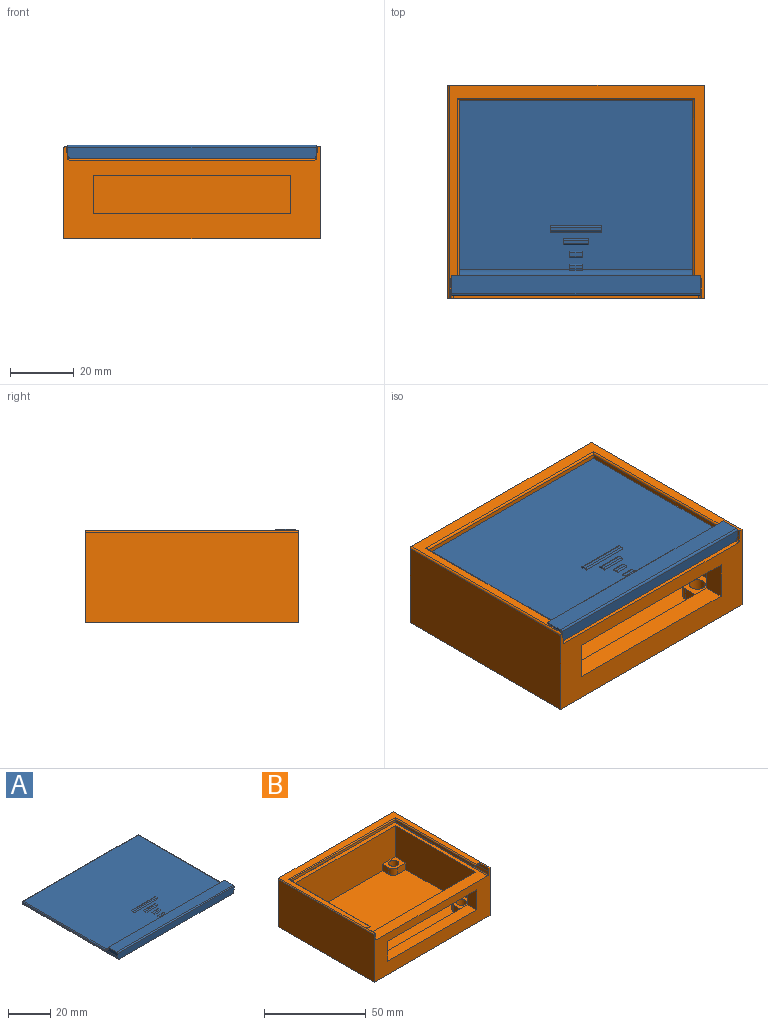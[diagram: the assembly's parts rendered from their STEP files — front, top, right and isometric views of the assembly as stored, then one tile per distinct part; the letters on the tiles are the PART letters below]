
ASSEMBLY  parts=2 mates=1
PART A: 39 faces, bbox 78.7x71.2x4.3 mm
  f0: plane 76.84x55.4mm, normal (0,0,1), area 4194.1mm2, adj f7,f8,f10,f11,f13,f14,f16,f17
  f1: plane 78x3.66mm, normal (0,-1,0), area 284.3mm2, adj f3,f4,f5,f26,f27,f29,f30,f32
  f2: plane 77.9x1.56mm, normal (0,1,0), area 116.2mm2, adj f3,f4,f5,f26,f27,f35,f36,f38
  f3: plane 75.68x64.2mm, normal (0,0,-1), area 4858.5mm2, adj f1,f2,f26,f27
  f4: plane 64.2x1.15mm, normal (-0.99,0,-0.15), area 41.5mm2, adj f1,f2,f27,f29,f34,f35
  f5: plane 64.2x1.15mm, normal (0.99,0,-0.15), area 41.5mm2, adj f1,f2,f26,f30,f37,f38
  f6: plane 4x1mm, normal (0,0,1), area 4mm2, adj f7,f8,f24,f25
  f7: plane 2x0.5mm, normal (-1,0,0), area 0.9mm2, adj f0,f6,f24,f25,f33
  f8: plane 2x0.5mm, normal (1,0,0), area 0.9mm2, adj f0,f6,f24,f25,f33
  f9: plane 4x1mm, normal (0,0,1), area 4mm2, adj f10,f11,f22,f23
  f10: plane 2x0.5mm, normal (-1,0,0), area 0.9mm2, adj f0,f9,f22,f23
  f11: plane 2x0.5mm, normal (1,0,0), area 0.9mm2, adj f0,f9,f22,f23
  f12: plane 8x1mm, normal (0,0,1), area 8mm2, adj f13,f14,f20,f21
  f13: plane 2x0.5mm, normal (-1,0,0), area 0.9mm2, adj f0,f12,f20,f21
  f14: plane 2x0.5mm, normal (1,0,0), area 0.9mm2, adj f0,f12,f20,f21
  f15: plane 16x1mm, normal (0,0,1), area 16mm2, adj f16,f17,f18,f19
  f16: plane 2x0.5mm, normal (-1,0,0), area 0.9mm2, adj f0,f15,f18,f19
  f17: plane 2x0.5mm, normal (1,0,0), area 0.9mm2, adj f0,f15,f18,f19
  f18: cylinder r=0.5mm len=16mm, axis (1,0,0), area 12.6mm2, adj f0,f15,f16,f17
  f19: cylinder r=0.5mm len=16mm, axis (-1,0,0), area 12.6mm2, adj f0,f15,f16,f17
  f20: cylinder r=0.5mm len=8mm, axis (1,0,0), area 6.3mm2, adj f0,f12,f13,f14
  f21: cylinder r=0.5mm len=8mm, axis (-1,0,0), area 6.3mm2, adj f0,f12,f13,f14
  f22: cylinder r=0.5mm len=4mm, axis (1,0,0), area 3.1mm2, adj f0,f9,f10,f11
  f23: cylinder r=0.5mm len=4mm, axis (-1,0,0), area 3.1mm2, adj f0,f9,f10,f11
  f24: cylinder r=0.5mm len=4mm, axis (1,0,0), area 3.1mm2, adj f0,f6,f7,f8
  f25: cylinder r=0.5mm len=4mm, axis (-1,0,0), area 3.1mm2, adj f6,f7,f8,f33
  f26: bspline ~71.17x0.99mm, area 93.2mm2, adj f1,f2,f3,f5
  f27: bspline ~71.17x0.99mm, area 93.2mm2, adj f1,f2,f3,f4
  f28: plane 77.94x0.26mm, normal (0,1,0), area 19.9mm2, adj f31,f33,f34,f37
  f29: plane 6.78x2.26mm, normal (-1,0,0), area 14.4mm2, adj f1,f4,f31,f32,f34
  f30: plane 6.78x2.26mm, normal (1,0,0), area 14.4mm2, adj f1,f5,f31,f32,f37
  f31: plane 78x5.7mm, normal (0,0,1), area 444.6mm2, adj f28,f29,f30,f32,f34,f37
  f32: cylinder r=0.6mm len=78mm, axis (-1,0,0), area 73.5mm2, adj f1,f29,f30,f31
  f33: cylinder r=2mm len=77.59mm, axis (-1,0,0), area 241.4mm2, adj f0,f7,f8,f25,f28,f34,f37
  f34: bspline ~2.85x2.5mm, area 2.1mm2, adj f4,f28,f29,f31,f33,f35
  f35: cylinder r=0.5mm len=55.9mm, axis (0,-1,0), area 47.9mm2, adj f0,f2,f4,f34,f36
  f36: cylinder r=0.5mm len=77.84mm, axis (1,0,0), area 60.7mm2, adj f0,f2,f35,f38
  f37: bspline ~2.85x2.5mm, area 2.1mm2, adj f5,f28,f30,f31,f33,f38
  f38: cylinder r=0.5mm len=55.9mm, axis (0,1,0), area 47.9mm2, adj f0,f2,f5,f36,f37
PART B: 63 faces, bbox 80.4x66.8x29.3 mm
  f0: plane 77.28x55.75mm, normal (0,0,-1), area 395.9mm2, adj f37,f38,f39,f49,f50,f59,f60,f62
  f1: plane 79.81x66.81mm, normal (0,0,1), area 633mm2, adj f35,f40,f42,f47,f48,f49,f50,f51
  f2: plane 55.9x22.7mm, normal (-1,0,0), area 1201.3mm2, adj f3,f5,f7,f9,f20,f21,f26,f31
  f3: plane 73.2x22.7mm, normal (0,1,0), area 849.6mm2, adj f2,f4,f6,f7,f17,f18,f26,f31
  f4: plane 55.9x22.7mm, normal (1,0,0), area 1201.3mm2, adj f3,f5,f6,f8,f14,f15,f26,f31
  f5: plane 73.2x22.7mm, normal (0,-1,0), area 1591.2mm2, adj f2,f4,f8,f9,f23,f24,f26,f31
  f6: plane 9.47x8.81mm, normal (0,0,1), area 61.1mm2, adj f3,f4,f12,f15,f16,f17
  f7: plane 9.47x8.81mm, normal (0,0,1), area 61.1mm2, adj f2,f3,f18,f19,f20,f27
  f8: plane 8.81x7.43mm, normal (0,0,1), area 43.1mm2, adj f4,f5,f10,f14,f24,f25
  f9: plane 8.81x7.43mm, normal (0,0,1), area 43.1mm2, adj f2,f5,f21,f22,f23,f29
  f10: cylinder r=2.55mm len=5.1mm, axis (0,0,1), area 80.1mm2, adj f8,f11
  f11: plane 5.1x5.1mm, normal (0,0,1), area 20.4mm2, adj f10
  f12: cylinder r=2.55mm len=5.1mm, axis (0,0,1), area 80.1mm2, adj f6,f13
  f13: plane 5.1x5.1mm, normal (0,0,1), area 20.4mm2, adj f12
  f14: plane 5.81x4mm, normal (0,-1,0), area 23.2mm2, adj f4,f8,f25,f26
  f15: plane 5.81x4mm, normal (0,1,0), area 23.2mm2, adj f4,f6,f16,f26
  f16: cylinder r=3mm len=4mm, axis (0,0,1), area 18.8mm2, adj f6,f15,f17,f26
  f17: plane 6.47x4mm, normal (1,0,0), area 25.9mm2, adj f3,f6,f16,f26
  f18: plane 6.47x4mm, normal (-1,0,0), area 25.9mm2, adj f3,f7,f19,f26
  f19: cylinder r=3mm len=4mm, axis (0,0,1), area 18.8mm2, adj f7,f18,f20,f26
  f20: plane 5.81x4mm, normal (0,1,0), area 23.2mm2, adj f2,f7,f19,f26
  f21: plane 5.81x4mm, normal (0,-1,0), area 23.2mm2, adj f2,f9,f22,f26
  f22: cylinder r=3mm len=4mm, axis (0,0,1), area 18.8mm2, adj f9,f21,f23,f26
  f23: plane 4.43x4mm, normal (-1,0,0), area 17.7mm2, adj f5,f9,f22,f26
  f24: plane 4.43x4mm, normal (1,0,0), area 17.7mm2, adj f5,f8,f25,f26
  f25: cylinder r=3mm len=4mm, axis (0,0,1), area 18.8mm2, adj f8,f14,f24,f26
  f26: plane 73.2x55.9mm, normal (0,0,1), area 3801.8mm2, adj f2,f3,f4,f5,f14,f15,f16,f17
  f27: cylinder r=2.55mm len=5.1mm, axis (0,0,1), area 80.1mm2, adj f7,f28
  f28: plane 5.1x5.1mm, normal (0,0,1), area 20.4mm2, adj f27
  f29: cylinder r=2.55mm len=5.1mm, axis (0,0,1), area 80.1mm2, adj f9,f30
  f30: plane 5.1x5.1mm, normal (0,0,1), area 20.4mm2, adj f29
  f31: plane 76.94x64.5mm, normal (0,0,1), area 870.9mm2, adj f2,f3,f4,f5,f42,f55,f56,f57
  f32: plane 65x1.86mm, normal (-0.99,0,0.13), area 89.5mm2, adj f34,f42,f48,f56,f57,f61,f62
  f33: plane 65x1.86mm, normal (0.99,0,0.13), area 89.5mm2, adj f34,f42,f47,f55,f56,f58,f59
  f34: plane 78.28x1.3mm, normal (0,-1,0), area 101.6mm2, adj f32,f33,f56,f59,f60,f62
  f35: plane 80.4x29mm, normal (0,1,0), area 2331.5mm2, adj f1,f36,f40,f41,f54
  f36: plane 66.8x28.4mm, normal (-1,0,0), area 1897.1mm2, adj f35,f41,f42,f54
  f37: plane 73.2x1.4mm, normal (0,-1,0), area 102.5mm2, adj f0,f38,f39,f52
  f38: plane 55.7x1.4mm, normal (1,0,0), area 77.1mm2, adj f0,f37,f50,f53
  f39: plane 55.7x1.4mm, normal (-1,0,0), area 77.1mm2, adj f0,f37,f49,f51
  f40: plane 66.8x29mm, normal (1,0,0), area 1937.2mm2, adj f1,f35,f41,f42
  f41: plane 80.4x66.8mm, normal (0,0,-1), area 5370.7mm2, adj f35,f36,f40,f42
  f42: plane 80.4x29mm, normal (0,-1,0), area 1253.5mm2, adj f1,f31,f32,f33,f36,f40,f41,f43
  f43: plane 61.8x6.3mm, normal (0,0,1), area 389.3mm2, adj f3,f42,f44,f45
  f44: plane 12x6.3mm, normal (1,0,0), area 75.6mm2, adj f3,f42,f43,f46
  f45: plane 12x6.3mm, normal (-1,0,0), area 75.6mm2, adj f3,f42,f43,f46
  f46: plane 61.8x6.3mm, normal (0,0,-1), area 389.3mm2, adj f3,f42,f44,f45
  f47: plane 7.07x2mm, normal (1,0,0), area 13.1mm2, adj f1,f33,f42,f58
  f48: plane 7.07x2mm, normal (-1,0,0), area 13.1mm2, adj f1,f32,f42,f61
  f49: cylinder r=2.5mm len=2.45mm, axis (-1,0,0), area 7.3mm2, adj f0,f1,f39,f51,f61
  f50: cylinder r=2.5mm len=2.45mm, axis (-1,0,0), area 7.3mm2, adj f0,f1,f38,f53,f58
  f51: cylinder r=0.6mm len=56.5mm, axis (0,1,0), area 52.9mm2, adj f1,f39,f49,f52
  f52: cylinder r=0.6mm len=74.4mm, axis (-1,0,0), area 69.6mm2, adj f1,f37,f51,f53
  f53: cylinder r=0.6mm len=56.5mm, axis (0,-1,0), area 52.9mm2, adj f1,f38,f50,f52
  f54: cylinder r=0.6mm len=66.8mm, axis (0,1,0), area 63mm2, adj f1,f35,f36,f42
  f55: cylinder r=0.5mm len=65mm, axis (0,1,0), area 46.7mm2, adj f31,f33,f42,f56
  f56: cylinder r=0.5mm len=77.95mm, axis (1,0,0), area 60.9mm2, adj f31,f32,f33,f34,f55,f57
  f57: cylinder r=0.5mm len=65mm, axis (0,-1,0), area 46.7mm2, adj f31,f32,f42,f56
  f58: bspline ~3.51x2.85mm, area 2.3mm2, adj f1,f33,f47,f50,f59
  f59: cylinder r=0.5mm len=56.25mm, axis (0,-1,0), area 47.7mm2, adj f0,f33,f34,f58,f60
  f60: cylinder r=0.5mm len=78.28mm, axis (-1,0,0), area 61.1mm2, adj f0,f34,f59,f62
  f61: bspline ~2.99x2.85mm, area 2.3mm2, adj f1,f32,f48,f49,f62
  f62: cylinder r=0.5mm len=56.25mm, axis (0,1,0), area 47.7mm2, adj f0,f32,f34,f60,f61
PLACE A t=(137.46,-130.22,-28.84)mm
PLACE B t=(137.46,-132.27,-53.94)mm
MATE fastened B.f34 <-> A.f2  axis (0,-1,0) through (137.46,-98.37,-28.09)mm
